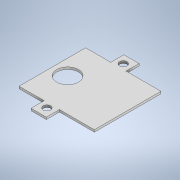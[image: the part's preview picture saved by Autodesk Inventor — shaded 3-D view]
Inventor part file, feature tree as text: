
AUTODESK INVENTOR PART (.ipt)
format: ipt  version: 2020.2 (Build 242310000, 310)  size: 181,248 bytes
history: native  units: mm
features: sketch x5, extrude x4, projected_geometry x2, hole x1
ambient origin geometry x8: Origin, YZ Plane, XZ Plane, XY Plane, X Axis, Y Axis, Z Axis, Center Point
bodies: Solid1 (feature_tree)
feature tree (12):
  extrude  "Extrusion1"  Depth=30.48mm
  extrude  "Extrusion2"  Depth=1.0mm
  extrude  "Extrusion3"  Depth=1.0mm
  hole  "Hole1"  [1 undecoded]
  extrude  "Extrusion4"  Depth=7.0mm
  sketch  "Sketch1"  dims[d0=34.5mm d1=30.48mm]
  sketch  "Sketch2"  dims[d2=1.0mm d3=0.0mm d4=1.0mm]
  projected_geometry  "Projected Loop1"
  sketch  "Sketch3"  dims[d5=1.0mm d6=1.0mm]
  sketch  "Sketch4"  dims[d7=1.0mm d8=2.0mm d9=0.0mm]
  sketch  "Sketch5"  dims[d10=14.0mm d11=17.5mm d12=35.0mm d13=3.4mm d14=3.4mm d15=3.5mm d16=7.0mm d17=7.0mm d18=7.0mm d19=1.0mm d20=0.0mm d21=6.0mm d22=10.0mm d23=6.0mm d24=6.3mm d25=2.0mm d26=90.0deg d27=8.0mm d28=20.594885mm d29=2.0mm d30=0.0mm d31=7.0mm]
  projected_geometry  "Projected Loop2"
note: 1 required parameter value undecoded (feature->parameter linkage not recoverable at this tier; creation-order binding heuristic only, values carry confidence <= 0.55)
